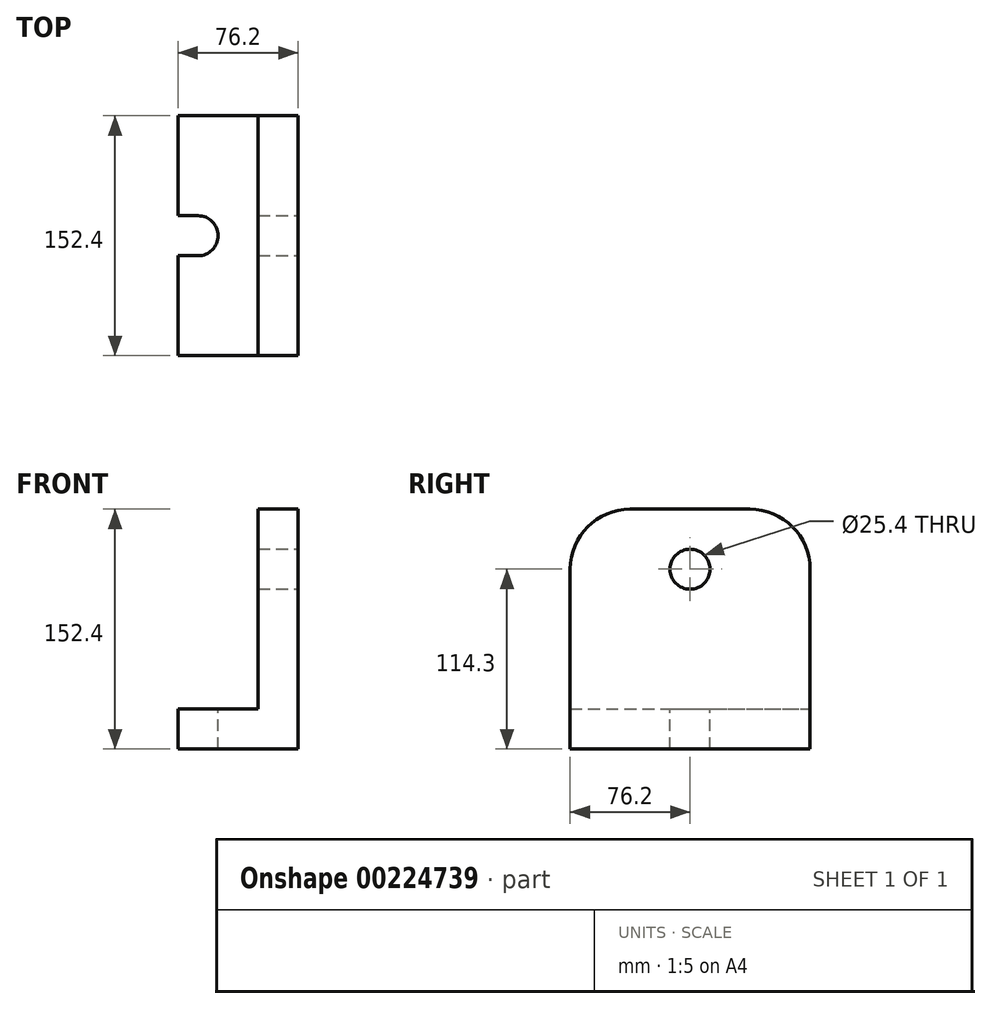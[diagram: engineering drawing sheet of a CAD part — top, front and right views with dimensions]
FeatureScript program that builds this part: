
annotation { "Feature Type Name" : "Feature", "Feature Type Description" : "" }
export const myFeature = defineFeature(function(context is Context, id is Id, definition is map)
    precondition{}
    {
        {
            var Q0;
            Q0=qCreatedBy(makeId("Front.planeOp"),FACE);
            var sketch = newSketch(context, id + "F0", { "sketchPlane" : qUnion([Q0])});
            skLineSegment(sketch, "E0", {"start": v(-76.2, 0) * mm, "end": v(0, 0) * mm});
            skLineSegment(sketch, "E1", {"start": v(0, 0) * mm, "end": v(0, 152.4) * mm});
            skLineSegment(sketch, "E2", {"start": v(0, 152.4) * mm, "end": v(-25.4, 152.4) * mm});
            skLineSegment(sketch, "E3", {"start": v(-25.4, 152.4) * mm, "end": v(-25.4, 25.4) * mm});
            skLineSegment(sketch, "E4", {"start": v(-25.4, 25.4) * mm, "end": v(-76.2, 25.4) * mm});
            skLineSegment(sketch, "E5", {"start": v(-76.2, 25.4) * mm, "end": v(-76.2, 0) * mm});
            skSolve(sketch);
        }
        {
            var Q0;
            Q0 = qSketchRegion(id + "F0", true);
            extrude(context, id + "F1", {"entities" : qUnion([Q0]), "endBound" : BoundingType.SYMMETRIC, "depth" : 152.4 * mm});
        }
        {
            var Q0;
            Q0=makeQuery(id+"F1.opExtrude","SWEPT_FACE",FACE,{"disambiguationData":[OSD([sQuery(id+"F0.wireOp",EDGE,"E1")])]});
            var sketch = newSketch(context, id + "F2", { "sketchPlane" : qUnion([Q0])});
            skCircle(sketch, "E6", {"center": v(0, 114.3) * mm, "radius": 12.7 * mm});
            skSolve(sketch);
        }
        {
            var Q0;
            Q0 = qSketchRegion(id + "F2", true);
            extrude(context, id + "F3", {"entities" : qUnion([Q0]), "operationType" : NewBodyOperationType.REMOVE, "endBound" : BoundingType.THROUGH_ALL, "oppositeDirection" : true, "depth" : 25.4 * mm});
        }
        {
            var Q0;
            Q0=makeQuery(id+"F1.opExtrude","SWEPT_FACE",FACE,{"disambiguationData":[OSD([sQuery(id+"F0.wireOp",EDGE,"E4")])]});
            var sketch = newSketch(context, id + "F4", { "sketchPlane" : qUnion([Q0])});
            skLineSegment(sketch, "E7.bottom", {"start": v(-76.2, 12.7) * mm, "end": v(-63.5, 12.7) * mm});
            skLineSegment(sketch, "E7.top", {"start": v(-76.2, -12.7) * mm, "end": v(-63.5, -12.7) * mm});
            skLineSegment(sketch, "E7.left", {"start": v(-76.2, 12.7) * mm, "end": v(-76.2, -12.7) * mm});
            skLineSegment(sketch, "E7.right", {"start": v(-63.5, 12.7) * mm, "end": v(-63.5, -12.7) * mm});
            skPoint(sketch, "E7.middle", {"position": v(-69.85, 0) * mm});
            skArc(sketch, "E8", {"start": v(-63.5, -12.7) * mm, "mid": v(-50.8, 0) * mm, "end": v(-63.5, 12.7) * mm});
            skSolve(sketch);
        }
        {
            var Q0;
            Q0=makeQuery(id+"F4.imprint","IMPRINT",FACE,{"disambiguationData":[TD([[makeQuery(id+"F4.imprint","IMPRINT",EDGE,{"derivedFrom":sQuery(id+"F4.wireOp",EDGE,"E7.bottom")}),-1.0]])]});
            var Q1;
            Q1=makeQuery(id+"F4.imprint","IMPRINT",FACE,{"disambiguationData":[TD([[makeQuery(id+"F4.imprint","IMPRINT",EDGE,{"derivedFrom":sQuery(id+"F4.wireOp",EDGE,"E7.right")}),1.0]])]});
            extrude(context, id + "F5", {"entities" : qUnion([Q0, Q1]), "operationType" : NewBodyOperationType.REMOVE, "endBound" : BoundingType.THROUGH_ALL, "oppositeDirection" : true, "depth" : 25.4 * mm});
        }
        {
            var Q0;
            Q0=makeQuery(id+"F1.opExtrude","CAP_EDGE",EDGE,{"disambiguationData":[OSD([sQuery(id+"F0.wireOp",EDGE,"E2")])],"isStart":true});
            var Q1;
            Q1=makeQuery(id+"F1.opExtrude","CAP_EDGE",EDGE,{"disambiguationData":[OSD([sQuery(id+"F0.wireOp",EDGE,"E2")])],"isStart":false});
            fillet(context, id + "F6", {"entities" : qUnion([Q0, Q1]), "radius" : 38.1 * mm, "tangentPropagation" : true, "allowEdgeOverflow" : false});
        }
    });
